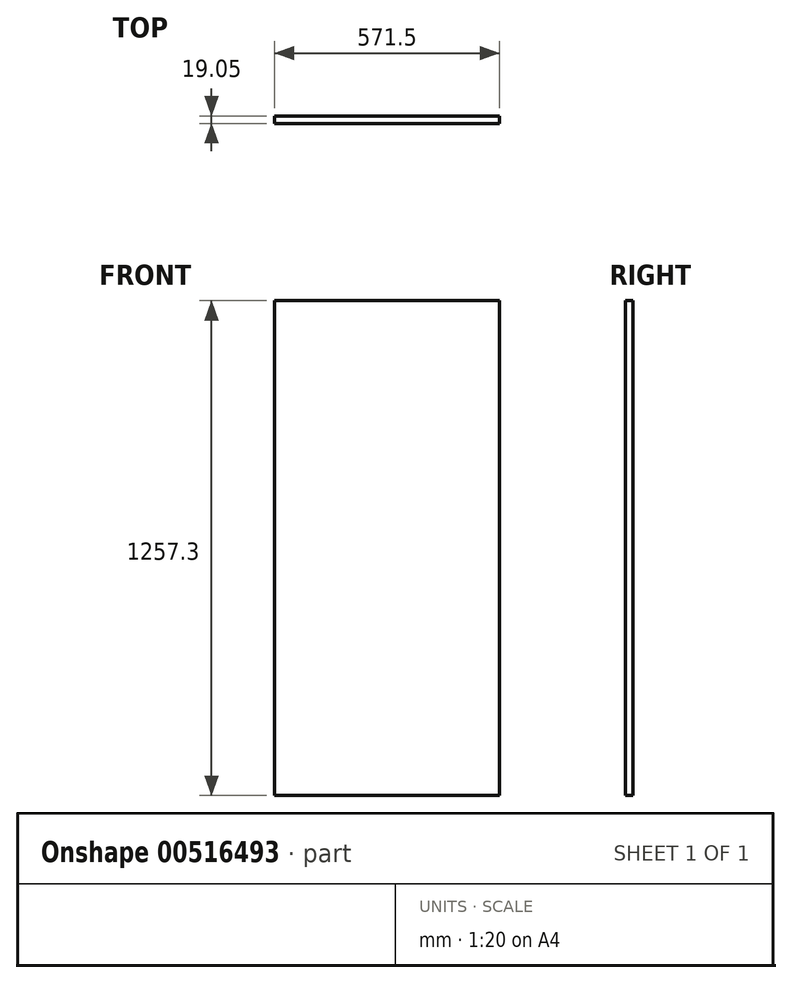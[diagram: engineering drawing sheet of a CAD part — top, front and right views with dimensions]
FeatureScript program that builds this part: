
annotation { "Feature Type Name" : "Feature", "Feature Type Description" : "" }
export const myFeature = defineFeature(function(context is Context, id is Id, definition is map)
    precondition{}
    {
        {
            var Q0;
            Q0=qCreatedBy(makeId("Front.planeOp"),FACE);
            var sketch = newSketch(context, id + "F0", { "sketchPlane" : qUnion([Q0])});
            skLineSegment(sketch, "E0.bottom", {"start": v(285.75, 628.65) * mm, "end": v(-285.75, 628.65) * mm});
            skLineSegment(sketch, "E0.top", {"start": v(285.75, -628.65) * mm, "end": v(-285.75, -628.65) * mm});
            skLineSegment(sketch, "E0.left", {"start": v(285.75, 628.65) * mm, "end": v(285.75, -628.65) * mm});
            skLineSegment(sketch, "E0.right", {"start": v(-285.75, 628.65) * mm, "end": v(-285.75, -628.65) * mm});
            skPoint(sketch, "E0.middle", {"position": v(0, 0) * mm});
            skSolve(sketch);
        }
        {
            var Q0;
            Q0 = qSketchRegion(id + "F0", true);
            extrude(context, id + "F1", {"entities" : qUnion([Q0]), "depth" : 19.05 * mm, "offsetDistance" : 25.4 * mm});
        }
    });
